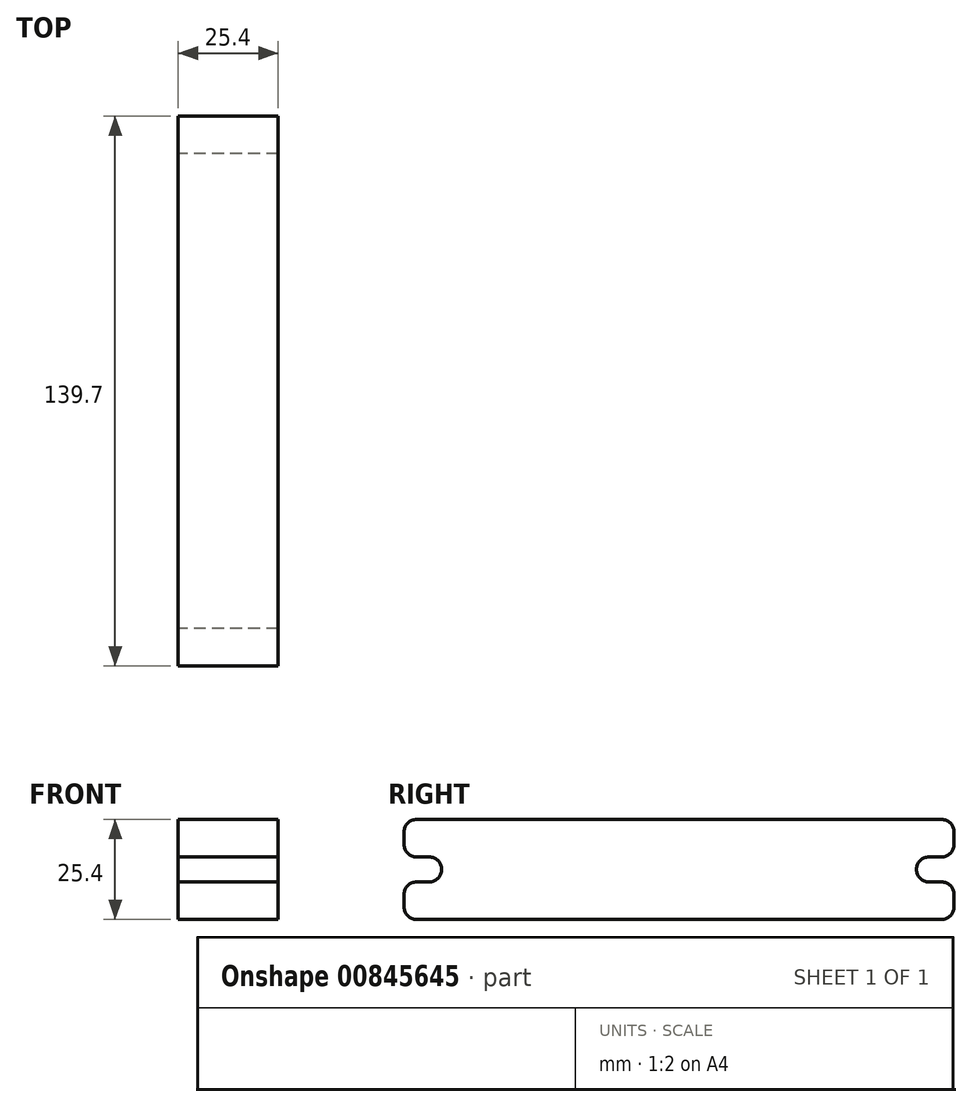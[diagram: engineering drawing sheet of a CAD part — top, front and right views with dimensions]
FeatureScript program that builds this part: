
annotation { "Feature Type Name" : "Feature", "Feature Type Description" : "" }
export const myFeature = defineFeature(function(context is Context, id is Id, definition is map)
    precondition{}
    {
        {
            var Q0;
            Q0=qCreatedBy(makeId("Right.planeOp"),FACE);
            var sketch = newSketch(context, id + "F0", { "sketchPlane" : qUnion([Q0])});
            skLineSegment(sketch, "E0.bottom", {"start": v(-66.68, 12.7) * mm, "end": v(66.68, 12.7) * mm});
            skLineSegment(sketch, "E0.top", {"start": v(-66.68, -12.7) * mm, "end": v(66.68, -12.7) * mm});
            skLineSegment(sketch, "E0.left", {"start": v(-69.85, 9.53) * mm, "end": v(-69.85, 6.35) * mm});
            skLineSegment(sketch, "E0.right", {"start": v(69.85, 9.53) * mm, "end": v(69.85, 6.35) * mm});
            skPoint(sketch, "E0.middle", {"position": v(0, 0) * mm});
            skLineSegment(sketch, "E1.bottom", {"start": v(-63.5, -3.17) * mm, "end": v(-66.68, -3.17) * mm});
            skLineSegment(sketch, "E1.top", {"start": v(-63.5, 3.18) * mm, "end": v(-66.68, 3.18) * mm});
            skLineSegment(sketch, "E1.left", {"start": v(-60.33, 0) * mm, "end": v(-60.33, 0) * mm});
            skPoint(sketch, "E1.middle", {"position": v(-69.85, 0) * mm});
            skLineSegment(sketch, "E2.trimOffspring", {"start": v(-69.85, -6.35) * mm, "end": v(-69.85, -9.53) * mm});
            skPoint(sketch, "E3.orphan", {"position": v(-79.38, 3.18) * mm});
            skPoint(sketch, "E4.orphan", {"position": v(-79.38, -3.17) * mm});
            skPoint(sketch, "E5.visualSharp", {"position": v(69.85, 12.7) * mm});
            skArc(sketch, "E5.filletArc", {"start": v(69.85, 9.53) * mm, "mid": v(68.92, 11.77) * mm, "end": v(66.68, 12.7) * mm});
            skPoint(sketch, "E6.visualSharp", {"position": v(69.85, 3.18) * mm});
            skArc(sketch, "E6.filletArc", {"start": v(66.68, 3.18) * mm, "mid": v(68.92, 4.1) * mm, "end": v(69.85, 6.35) * mm});
            skPoint(sketch, "E7.visualSharp", {"position": v(69.85, -12.7) * mm});
            skArc(sketch, "E7.filletArc", {"start": v(66.68, -12.7) * mm, "mid": v(68.92, -11.77) * mm, "end": v(69.85, -9.53) * mm});
            skPoint(sketch, "E8.visualSharp", {"position": v(-69.85, -3.17) * mm});
            skArc(sketch, "E8.filletArc", {"start": v(-66.68, -3.17) * mm, "mid": v(-68.92, -4.1) * mm, "end": v(-69.85, -6.35) * mm});
            skPoint(sketch, "E9.visualSharp", {"position": v(-69.85, -12.7) * mm});
            skArc(sketch, "E9.filletArc", {"start": v(-69.85, -9.53) * mm, "mid": v(-68.92, -11.77) * mm, "end": v(-66.68, -12.7) * mm});
            skPoint(sketch, "E10.visualSharp", {"position": v(-69.85, 3.18) * mm});
            skArc(sketch, "E10.filletArc", {"start": v(-69.85, 6.35) * mm, "mid": v(-68.92, 4.1) * mm, "end": v(-66.68, 3.18) * mm});
            skPoint(sketch, "E11.visualSharp", {"position": v(-69.85, 12.7) * mm});
            skArc(sketch, "E11.filletArc", {"start": v(-66.68, 12.7) * mm, "mid": v(-68.92, 11.77) * mm, "end": v(-69.85, 9.53) * mm});
            skPoint(sketch, "E12.visualSharp", {"position": v(-60.33, 3.18) * mm});
            skArc(sketch, "E12.filletArc", {"start": v(-60.33, 0) * mm, "mid": v(-61.25, 2.25) * mm, "end": v(-63.5, 3.18) * mm});
            skPoint(sketch, "E13.visualSharp", {"position": v(-60.33, -3.17) * mm});
            skArc(sketch, "E13.filletArc", {"start": v(-63.5, -3.17) * mm, "mid": v(-61.25, -2.25) * mm, "end": v(-60.33, 0) * mm});
            skPoint(sketch, "E14.visualSharp", {"position": v(60.33, 3.18) * mm});
            skLineSegment(sketch, "E15.MirrorCS", {"start": v(-63.5, 3.17) * mm, "end": v(-66.68, 3.17) * mm});
            skLineSegment(sketch, "E16.MirrorCS", {"start": v(-63.5, -3.18) * mm, "end": v(-66.68, -3.18) * mm});
            skArc(sketch, "E17.MirrorCS", {"start": v(-63.5, 3.17) * mm, "mid": v(-61.25, 2.25) * mm, "end": v(-60.33, 0) * mm});
            skArc(sketch, "E18.MirrorCS", {"start": v(-60.33, 0) * mm, "mid": v(-61.25, -2.25) * mm, "end": v(-63.5, -3.18) * mm});
            skPoint(sketch, "E19.MirrorP", {"position": v(-69.85, -3.18) * mm});
            skPoint(sketch, "E20.MirrorP", {"position": v(-69.85, 3.17) * mm});
            skPoint(sketch, "E21.MirrorP", {"position": v(-60.33, 3.17) * mm});
            skPoint(sketch, "E22.MirrorP", {"position": v(-60.33, -3.18) * mm});
            skArc(sketch, "E23.MirrorCS", {"start": v(-66.68, 3.17) * mm, "mid": v(-68.92, 4.1) * mm, "end": v(-69.85, 6.35) * mm});
            skLineSegment(sketch, "E24.MirrorCS", {"start": v(-69.85, 6.35) * mm, "end": v(-69.85, 9.53) * mm});
            skPoint(sketch, "E25.MirrorP", {"position": v(-79.38, 3.17) * mm});
            skPoint(sketch, "E26.MirrorCS.start.orphan", {"position": v(60.33, -3.17) * mm});
            skPoint(sketch, "E27.MirrorCS.end.orphan", {"position": v(69.85, -3.17) * mm});
            skLineSegment(sketch, "E28.MirrorCS", {"start": v(63.5, 3.17) * mm, "end": v(66.68, 3.17) * mm});
            skArc(sketch, "E29.MirrorCS", {"start": v(63.5, 3.17) * mm, "mid": v(61.25, 2.25) * mm, "end": v(60.33, 0) * mm});
            skPoint(sketch, "E30.MirrorP", {"position": v(60.33, 3.17) * mm});
            skPoint(sketch, "E31.MirrorP", {"position": v(69.85, 3.17) * mm});
            skArc(sketch, "E32.MirrorCS", {"start": v(60.33, 0) * mm, "mid": v(61.25, 2.25) * mm, "end": v(63.5, 3.18) * mm});
            skLineSegment(sketch, "E33.MirrorCS", {"start": v(63.5, 3.18) * mm, "end": v(66.68, 3.18) * mm});
            skLineSegment(sketch, "E34.MirrorCS", {"start": v(60.33, 0) * mm, "end": v(60.33, 0) * mm});
            skPoint(sketch, "E35.MirrorP", {"position": v(69.85, 0) * mm});
            skArc(sketch, "E36.MirrorCS", {"start": v(60.33, 0) * mm, "mid": v(61.25, -2.25) * mm, "end": v(63.5, -3.18) * mm});
            skLineSegment(sketch, "E37.MirrorCS", {"start": v(63.5, -3.17) * mm, "end": v(66.68, -3.17) * mm});
            skPoint(sketch, "E38.MirrorP", {"position": v(69.85, -3.18) * mm});
            skArc(sketch, "E39.MirrorCS", {"start": v(66.68, 3.17) * mm, "mid": v(68.92, 4.1) * mm, "end": v(69.85, 6.35) * mm});
            skArc(sketch, "E40.MirrorCS", {"start": v(63.5, -3.17) * mm, "mid": v(61.25, -2.25) * mm, "end": v(60.33, 0) * mm});
            skArc(sketch, "E41.MirrorCS", {"start": v(66.68, -3.17) * mm, "mid": v(68.92, -4.1) * mm, "end": v(69.85, -6.35) * mm});
            skPoint(sketch, "E42.MirrorP", {"position": v(60.33, -3.18) * mm});
            skLineSegment(sketch, "E43.MirrorCS", {"start": v(69.85, 6.35) * mm, "end": v(69.85, 9.53) * mm});
            skLineSegment(sketch, "E44.MirrorCS", {"start": v(63.5, -3.18) * mm, "end": v(66.68, -3.18) * mm});
            skLineSegment(sketch, "E45.MirrorCS", {"start": v(69.85, -6.35) * mm, "end": v(69.85, -9.53) * mm});
            skArc(sketch, "E46.MirrorCS", {"start": v(69.85, 6.35) * mm, "mid": v(68.92, 4.1) * mm, "end": v(66.68, 3.18) * mm});
            skSolve(sketch);
        }
        {
            var Q0;
            Q0 = qSketchRegion(id + "F0", true);
            extrude(context, id + "F1", {"entities" : qUnion([Q0]), "depth" : 25.4 * mm, "offsetDistance" : 25.4 * mm});
        }
    });
